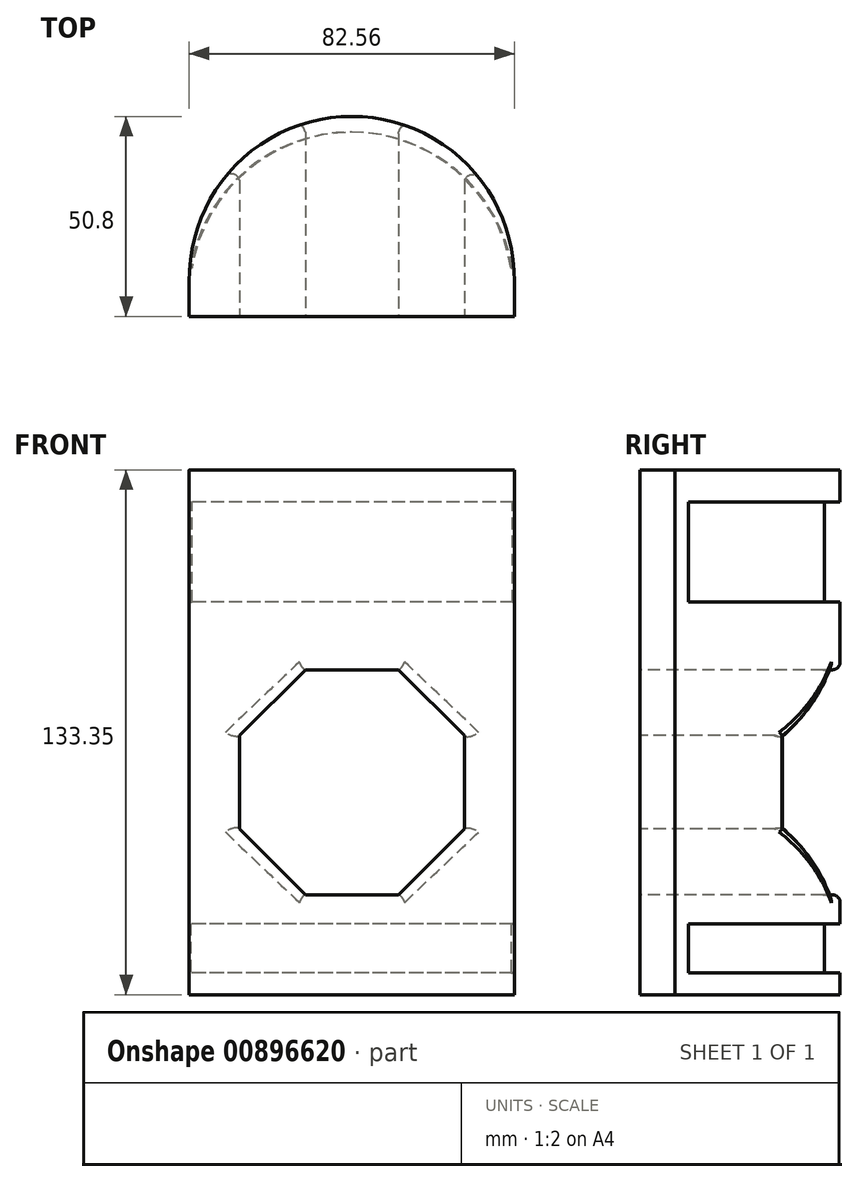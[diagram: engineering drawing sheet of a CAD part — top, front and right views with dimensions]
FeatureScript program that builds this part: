
annotation { "Feature Type Name" : "Feature", "Feature Type Description" : "" }
export const myFeature = defineFeature(function(context is Context, id is Id, definition is map)
    precondition{}
    {
        {
            var Q0;
            Q0=qCreatedBy(makeId("Top.planeOp"),FACE);
            var sketch = newSketch(context, id + "F0", { "sketchPlane" : qUnion([Q0])});
            skLineSegment(sketch, "E0.bottom", {"start": v(-0.06, -9.47) * mm, "end": v(41.22, -9.47) * mm});
            skLineSegment(sketch, "E0.left", {"start": v(-0.06, -9.47) * mm, "end": v(-0.06, 41.33) * mm});
            skLineSegment(sketch, "E0.right", {"start": v(41.22, -9.47) * mm, "end": v(41.22, -0.58) * mm});
            skArc(sketch, "E1", {"start": v(41.22, -0.58) * mm, "mid": v(29.35, 29.01) * mm, "end": v(-0.06, 41.33) * mm});
            skSolve(sketch);
        }
        {
            var Q0;
            Q0=makeQuery(id+"F0.imprint","IMPRINT",FACE,{"disambiguationData":[TD([[makeQuery(id+"F0.imprint","IMPRINT",EDGE,{"derivedFrom":sQuery(id+"F0.wireOp",EDGE,"E0.bottom")}),1.0]])]});
            extrude(context, id + "F1", {"entities" : qUnion([Q0]), "depth" : 133.35 * mm, "offsetDistance" : 25.4 * mm});
        }
        {
            var Q0;
            Q0=makeQuery(id+"F1.opExtrude","SWEPT_BODY",BODY,{"disambiguationData":[OSD([sQuery(id+"F0.wireOp",EDGE,"E0.bottom"),sQuery(id+"F0.wireOp",EDGE,"E0.left"),sQuery(id+"F0.wireOp",EDGE,"E0.right"),sQuery(id+"F0.wireOp",EDGE,"E1")])]});
            var Q1;
            Q1=makeQuery(id+"F1.opExtrude","SWEPT_FACE",FACE,{"disambiguationData":[OSD([sQuery(id+"F0.wireOp",EDGE,"E0.left")])]});
            mirror(context, id + "F2", {"operationType" : NewBodyOperationType.ADD, "entities" : qUnion([Q0]), "mirrorPlane" : qUnion([Q1])});
        }
        {
            var Q0;
            Q0=makeQuery(id+"F1.opExtrude","SWEPT_BODY",BODY,{"disambiguationData":[OSD([sQuery(id+"F0.wireOp",EDGE,"E0.bottom"),sQuery(id+"F0.wireOp",EDGE,"E0.left"),sQuery(id+"F0.wireOp",EDGE,"E0.right"),sQuery(id+"F0.wireOp",EDGE,"E1")])]});
            transform(context, id + "F3", {"entities" : qUnion([Q0]), "transformType" : TransformType.TRANSLATION_3D, "dx" : 0 * mm, "dy" : 0 * mm, "dz" : -125.22 * mm, "makeCopy" : false});
        }
        {
            var Q0;
            Q0=makeQuery(id+"F1.opExtrude","SWEPT_BODY",BODY,{"disambiguationData":[OSD([sQuery(id+"F0.wireOp",EDGE,"E0.bottom"),sQuery(id+"F0.wireOp",EDGE,"E0.left"),sQuery(id+"F0.wireOp",EDGE,"E0.right"),sQuery(id+"F0.wireOp",EDGE,"E1")])]});
            transform(context, id + "F4", {"entities" : qUnion([Q0]), "transformType" : TransformType.TRANSLATION_3D, "dx" : 0 * mm, "dy" : 0 * mm, "dz" : 0 * mm, "makeCopy" : false});
        }
        {
            var Q0;
            Q0=qCreatedBy(makeId("Top.planeOp"),FACE);
            var sketch = newSketch(context, id + "F5", { "sketchPlane" : qUnion([Q0])});
            skArc(sketch, "E2", {"start": v(41.53, 2.76) * mm, "mid": v(29.51, 32.51) * mm, "end": v(-0.18, 44.67) * mm});
            skArc(sketch, "E3.MirrorCS", {"start": v(-41.46, 2.76) * mm, "mid": v(-29.6, 32.36) * mm, "end": v(-0.18, 44.67) * mm});
            skArc(sketch, "E4", {"start": v(40.76, 2.76) * mm, "mid": v(26.74, 27.5) * mm, "end": v(0.03, 37.3) * mm});
            skArc(sketch, "E5.MirrorCS", {"start": v(-40.7, 2.76) * mm, "mid": v(-26.67, 27.5) * mm, "end": v(0.03, 37.3) * mm});
            skLineSegment(sketch, "E6", {"start": v(-41.46, 2.76) * mm, "end": v(-40.7, 2.76) * mm});
            skLineSegment(sketch, "E7.trimOffspring", {"start": v(40.76, 2.76) * mm, "end": v(41.53, 2.76) * mm});
            skSolve(sketch);
        }
        {
            var Q0;
            Q0=qSketchRegion(id+"F5",true);
            extrude(context, id + "F6", {"entities" : qUnion([Q0]), "operationType" : NewBodyOperationType.REMOVE, "oppositeDirection" : true, "depth" : 25.4 * mm, "offsetDistance" : 25.4 * mm});
        }
        {
            var Q0;
            Q0=makeQuery(id+"F1.opExtrude","SWEPT_BODY",BODY,{"disambiguationData":[OSD([sQuery(id+"F0.wireOp",EDGE,"E0.bottom"),sQuery(id+"F0.wireOp",EDGE,"E0.left"),sQuery(id+"F0.wireOp",EDGE,"E0.right"),sQuery(id+"F0.wireOp",EDGE,"E1")])]});
            transform(context, id + "F7", {"entities" : qUnion([Q0]), "transformType" : TransformType.TRANSLATION_3D, "dx" : 0 * mm, "dy" : 0 * mm, "dz" : 133.86 * mm, "makeCopy" : false});
        }
        {
            var Q0;
            Q0=qCreatedBy(makeId("Top.planeOp"),FACE);
            var sketch = newSketch(context, id + "F8", { "sketchPlane" : qUnion([Q0])});
            skArc(sketch, "E8", {"start": v(41.2, 2.77) * mm, "mid": v(29.18, 32.52) * mm, "end": v(-0.52, 44.68) * mm});
            skArc(sketch, "E9.MirrorCS", {"start": v(-41.8, 2.77) * mm, "mid": v(-29.93, 32.36) * mm, "end": v(-0.52, 44.68) * mm});
            skArc(sketch, "E10", {"start": v(40.43, 2.77) * mm, "mid": v(26.4, 27.51) * mm, "end": v(-0.3, 37.31) * mm});
            skArc(sketch, "E11.MirrorCS", {"start": v(-41.03, 2.77) * mm, "mid": v(-27, 27.51) * mm, "end": v(-0.3, 37.31) * mm});
            skLineSegment(sketch, "E12", {"start": v(-41.8, 2.77) * mm, "end": v(-41.03, 2.77) * mm});
            skLineSegment(sketch, "E13.trimOffspring", {"start": v(40.43, 2.77) * mm, "end": v(41.2, 2.77) * mm});
            skSolve(sketch);
        }
        {
            var Q0;
            Q0=makeQuery(id+"F1.opExtrude","SWEPT_BODY",BODY,{"disambiguationData":[OSD([sQuery(id+"F0.wireOp",EDGE,"E0.bottom"),sQuery(id+"F0.wireOp",EDGE,"E0.left"),sQuery(id+"F0.wireOp",EDGE,"E0.right"),sQuery(id+"F0.wireOp",EDGE,"E1")])]});
            transform(context, id + "F9", {"entities" : qUnion([Q0]), "transformType" : TransformType.TRANSLATION_3D, "dx" : 0 * mm, "dy" : 0 * mm, "dz" : -14.22 * mm, "makeCopy" : false});
        }
        {
            var Q0;
            Q0=qSketchRegion(id+"F8",true);
            extrude(context, id + "F10", {"entities" : qUnion([Q0]), "operationType" : NewBodyOperationType.REMOVE, "depth" : 12.45 * mm, "offsetDistance" : 25.4 * mm});
        }
        {
            var Q0;
            {var subQ0=makeQuery(id+"F1.opExtrude","SWEPT_FACE",FACE,{"disambiguationData":[OSD([sQuery(id+"F0.wireOp",EDGE,"E0.bottom")])]});Q0=makeQuery(id+"F2.boolean.opBoolean","MERGE",FACE,{"derivedFrom":[subQ0,makeQuery(id+"F2.opPattern","COPY",FACE,{"derivedFrom":subQ0,"instanceName":"1"})]});}
            var sketch = newSketch(context, id + "F11", { "sketchPlane" : qUnion([Q0])});
            skCircle(sketch, "E14.cCircle", {"center": v(0, 48.39) * mm, "radius": 28.58 * mm, "construction": true});
            skLineSegment(sketch, "E14.0", {"start": v(11.84, 19.81) * mm, "end": v(-11.84, 19.81) * mm});
            skLineSegment(sketch, "E14.1", {"start": v(-11.84, 19.81) * mm, "end": v(-28.58, 36.55) * mm});
            skLineSegment(sketch, "E14.2", {"start": v(-28.58, 36.55) * mm, "end": v(-28.58, 60.22) * mm});
            skLineSegment(sketch, "E14.3", {"start": v(-28.57, 60.22) * mm, "end": v(-11.84, 76.96) * mm});
            skLineSegment(sketch, "E14.4", {"start": v(-11.84, 76.96) * mm, "end": v(11.84, 76.96) * mm});
            skLineSegment(sketch, "E14.5", {"start": v(11.84, 76.96) * mm, "end": v(28.58, 60.22) * mm});
            skLineSegment(sketch, "E14.6", {"start": v(28.58, 60.22) * mm, "end": v(28.58, 36.55) * mm});
            skLineSegment(sketch, "E14.7", {"start": v(28.58, 36.55) * mm, "end": v(11.84, 19.81) * mm});
            skPoint(sketch, "E14.0.midPoint", {"position": v(0, 19.81) * mm});
            skSolve(sketch);
        }
        {
            var Q0;
            Q0 = qSketchRegion(id + "F11", true);
            extrude(context, id + "F12", {"entities" : qUnion([Q0]), "operationType" : NewBodyOperationType.REMOVE, "oppositeDirection" : true, "depth" : 53.85 * mm, "offsetDistance" : 25.4 * mm});
        }
        {
            var Q0;
            {var subQ0=makeQuery(id+"F1.opExtrude","SWEPT_FACE",FACE,{"disambiguationData":[OSD([sQuery(id+"F0.wireOp",EDGE,"E1")])]});Q0=makeQuery(id+"F12.boolean.opBoolean","INTERSECT",EDGE,{"derivedFrom":[makeQuery(id+"F2.boolean.opBoolean","MERGE",FACE,{"derivedFrom":[subQ0,makeQuery(id+"F2.opPattern","COPY",FACE,{"derivedFrom":subQ0,"instanceName":"1"})]}),makeQuery(id+"F12.opExtrude","SWEPT_FACE",FACE,{"disambiguationData":[OSD([sQuery(id+"F11.wireOp",EDGE,"E14.5")])]})]});}
            var Q1;
            {var subQ0=makeQuery(id+"F1.opExtrude","SWEPT_FACE",FACE,{"disambiguationData":[OSD([sQuery(id+"F0.wireOp",EDGE,"E1")])]});Q1=makeQuery(id+"F12.boolean.opBoolean","INTERSECT",EDGE,{"derivedFrom":[makeQuery(id+"F2.boolean.opBoolean","MERGE",FACE,{"derivedFrom":[subQ0,makeQuery(id+"F2.opPattern","COPY",FACE,{"derivedFrom":subQ0,"instanceName":"1"})]}),makeQuery(id+"F12.opExtrude","SWEPT_FACE",FACE,{"disambiguationData":[OSD([sQuery(id+"F11.wireOp",EDGE,"E14.4")])]})]});}
            var Q2;
            {var subQ0=makeQuery(id+"F1.opExtrude","SWEPT_FACE",FACE,{"disambiguationData":[OSD([sQuery(id+"F0.wireOp",EDGE,"E1")])]});Q2=makeQuery(id+"F12.boolean.opBoolean","INTERSECT",EDGE,{"derivedFrom":[makeQuery(id+"F2.boolean.opBoolean","MERGE",FACE,{"derivedFrom":[subQ0,makeQuery(id+"F2.opPattern","COPY",FACE,{"derivedFrom":subQ0,"instanceName":"1"})]}),makeQuery(id+"F12.opExtrude","SWEPT_FACE",FACE,{"disambiguationData":[OSD([sQuery(id+"F11.wireOp",EDGE,"E14.3")])]})]});}
            var Q3;
            {var subQ0=makeQuery(id+"F1.opExtrude","SWEPT_FACE",FACE,{"disambiguationData":[OSD([sQuery(id+"F0.wireOp",EDGE,"E1")])]});Q3=makeQuery(id+"F12.boolean.opBoolean","INTERSECT",EDGE,{"derivedFrom":[makeQuery(id+"F2.boolean.opBoolean","MERGE",FACE,{"derivedFrom":[subQ0,makeQuery(id+"F2.opPattern","COPY",FACE,{"derivedFrom":subQ0,"instanceName":"1"})]}),makeQuery(id+"F12.opExtrude","SWEPT_FACE",FACE,{"disambiguationData":[OSD([sQuery(id+"F11.wireOp",EDGE,"E14.2")])]})]});}
            var Q4;
            {var subQ0=makeQuery(id+"F1.opExtrude","SWEPT_FACE",FACE,{"disambiguationData":[OSD([sQuery(id+"F0.wireOp",EDGE,"E1")])]});Q4=makeQuery(id+"F12.boolean.opBoolean","INTERSECT",EDGE,{"derivedFrom":[makeQuery(id+"F2.boolean.opBoolean","MERGE",FACE,{"derivedFrom":[subQ0,makeQuery(id+"F2.opPattern","COPY",FACE,{"derivedFrom":subQ0,"instanceName":"1"})]}),makeQuery(id+"F12.opExtrude","SWEPT_FACE",FACE,{"disambiguationData":[OSD([sQuery(id+"F11.wireOp",EDGE,"E14.1")])]})]});}
            var Q5;
            {var subQ0=makeQuery(id+"F1.opExtrude","SWEPT_FACE",FACE,{"disambiguationData":[OSD([sQuery(id+"F0.wireOp",EDGE,"E1")])]});Q5=makeQuery(id+"F12.boolean.opBoolean","INTERSECT",EDGE,{"derivedFrom":[makeQuery(id+"F2.boolean.opBoolean","MERGE",FACE,{"derivedFrom":[subQ0,makeQuery(id+"F2.opPattern","COPY",FACE,{"derivedFrom":subQ0,"instanceName":"1"})]}),makeQuery(id+"F12.opExtrude","SWEPT_FACE",FACE,{"disambiguationData":[OSD([sQuery(id+"F11.wireOp",EDGE,"E14.0")])]})]});}
            var Q6;
            {var subQ0=makeQuery(id+"F1.opExtrude","SWEPT_FACE",FACE,{"disambiguationData":[OSD([sQuery(id+"F0.wireOp",EDGE,"E1")])]});Q6=makeQuery(id+"F12.boolean.opBoolean","INTERSECT",EDGE,{"derivedFrom":[makeQuery(id+"F2.boolean.opBoolean","MERGE",FACE,{"derivedFrom":[subQ0,makeQuery(id+"F2.opPattern","COPY",FACE,{"derivedFrom":subQ0,"instanceName":"1"})]}),makeQuery(id+"F12.opExtrude","SWEPT_FACE",FACE,{"disambiguationData":[OSD([sQuery(id+"F11.wireOp",EDGE,"E14.7")])]})]});}
            var Q7;
            {var subQ0=makeQuery(id+"F1.opExtrude","SWEPT_FACE",FACE,{"disambiguationData":[OSD([sQuery(id+"F0.wireOp",EDGE,"E1")])]});Q7=makeQuery(id+"F12.boolean.opBoolean","INTERSECT",EDGE,{"derivedFrom":[makeQuery(id+"F2.boolean.opBoolean","MERGE",FACE,{"derivedFrom":[subQ0,makeQuery(id+"F2.opPattern","COPY",FACE,{"derivedFrom":subQ0,"instanceName":"1"})]}),makeQuery(id+"F12.opExtrude","SWEPT_FACE",FACE,{"disambiguationData":[OSD([sQuery(id+"F11.wireOp",EDGE,"E14.6")])]})]});}
            fillet(context, id + "F13", {"entities" : qUnion([Q0, Q1, Q2, Q3, Q4, Q5, Q6, Q7]), "radius" : 2.03 * mm, "tangentPropagation" : true, "allowEdgeOverflow" : false});
        }
    });
